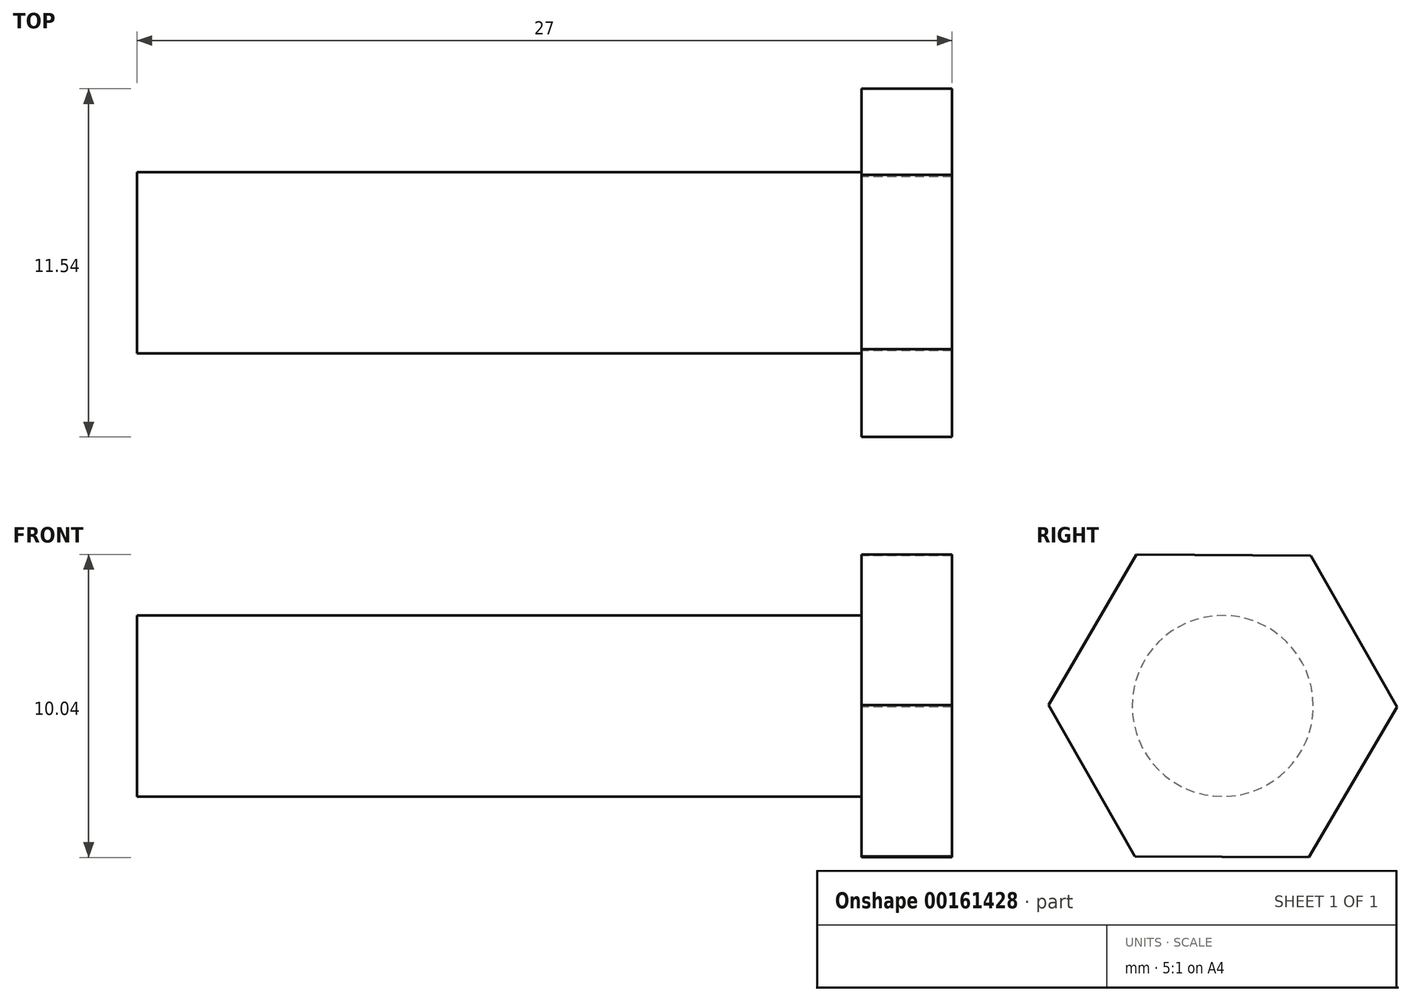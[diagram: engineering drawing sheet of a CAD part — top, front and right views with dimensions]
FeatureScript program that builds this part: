
annotation { "Feature Type Name" : "Feature", "Feature Type Description" : "" }
export const myFeature = defineFeature(function(context is Context, id is Id, definition is map)
    precondition{}
    {
        {
            var Q0;
            Q0=qCreatedBy(makeId("Right.planeOp"),FACE);
            var sketch = newSketch(context, id + "F0", { "sketchPlane" : qUnion([Q0])});
            skCircle(sketch, "E0.cCircle", {"center": v(0, 0) * mm, "radius": 5 * mm, "construction": true});
            skLineSegment(sketch, "E0.0", {"start": v(2.91, 4.98) * mm, "end": v(5.77, -0.03) * mm});
            skLineSegment(sketch, "E0.1", {"start": v(5.77, -0.03) * mm, "end": v(2.86, -5.02) * mm});
            skLineSegment(sketch, "E0.2", {"start": v(2.86, -5.02) * mm, "end": v(-2.91, -4.98) * mm});
            skLineSegment(sketch, "E0.3", {"start": v(-2.91, -4.98) * mm, "end": v(-5.77, 0.03) * mm});
            skLineSegment(sketch, "E0.4", {"start": v(-5.77, 0.03) * mm, "end": v(-2.86, 5.02) * mm});
            skLineSegment(sketch, "E0.5", {"start": v(-2.86, 5.02) * mm, "end": v(2.91, 4.98) * mm});
            skPoint(sketch, "E0.0.midPoint", {"position": v(4.34, 2.48) * mm});
            skSolve(sketch);
        }
        {
            var Q0;
            Q0 = qSketchRegion(id + "F0", true);
            var Q1;
            Q1 = qSketchRegion(id + "F2", true);
            extrude(context, id + "F1", {"entities" : qUnion([Q0, Q1]), "depth" : 3 * mm, "offsetDistance" : 25 * mm});
        }
        {
            var Q0;
            Q0=makeQuery(id+"F1.opExtrude","CAP_FACE",FACE,{"disambiguationData":[OSD([sQuery(id+"F0.wireOp",EDGE,"E0.0"),sQuery(id+"F0.wireOp",EDGE,"E0.1"),sQuery(id+"F0.wireOp",EDGE,"E0.2"),sQuery(id+"F0.wireOp",EDGE,"E0.3"),sQuery(id+"F0.wireOp",EDGE,"E0.4"),sQuery(id+"F0.wireOp",EDGE,"E0.5")])],"isStart":true});
            var sketch = newSketch(context, id + "F2", { "sketchPlane" : qUnion([Q0])});
            skCircle(sketch, "E1", {"center": v(0, 0) * mm, "radius": 3 * mm});
            skSolve(sketch);
        }
        {
            var Q0;
            Q0 = qSketchRegion(id + "F2", true);
            extrude(context, id + "F3", {"entities" : qUnion([Q0]), "operationType" : NewBodyOperationType.ADD, "depth" : 24 * mm, "offsetDistance" : 25 * mm});
        }
    });
